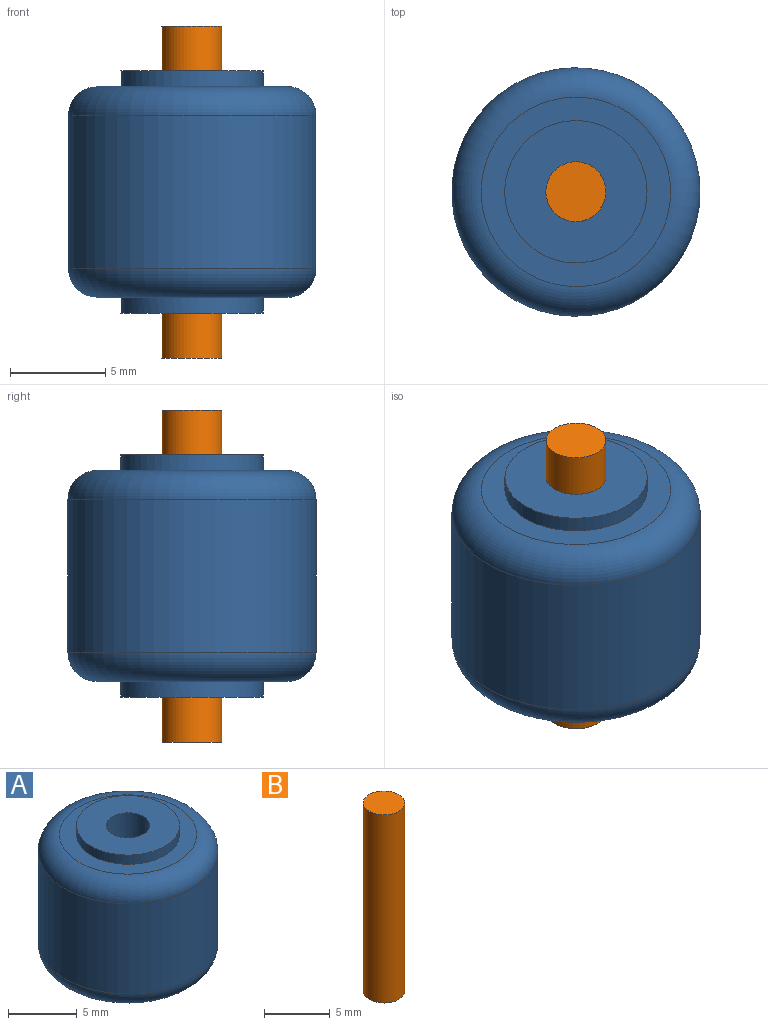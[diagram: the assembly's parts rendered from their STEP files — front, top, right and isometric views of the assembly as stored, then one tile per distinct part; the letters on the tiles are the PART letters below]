
ASSEMBLY  parts=2 mates=1
PART A: 10 faces, bbox 14.1x14.1x12.7 mm
  f0: cylinder r=6.52mm len=13.05mm, axis (0,0,-1), area 328.5mm2, adj f3,f4
  f1: plane 9.96x9.96mm, normal (0,0,1), area 34mm2, adj f4,f7
  f2: plane 9.96x9.96mm, normal (0,0,-1), area 34mm2, adj f3,f5
  f3: torus R=4.98mm, axis (0,0,1), area 90.8mm2, adj f0,f2
  f4: torus R=4.98mm, axis (0,0,1), area 90.8mm2, adj f0,f1
  f5: cylinder r=3.74mm len=7.48mm, axis (0,0,1), area 19.1mm2, adj f2,f6
  f6: plane 7.48x7.48mm, normal (0,0,-1), area 36.1mm2, adj f5,f9
  f7: cylinder r=3.74mm len=7.48mm, axis (0,0,-1), area 19.1mm2, adj f1,f8
  f8: plane 7.48x7.48mm, normal (0,0,1), area 36.1mm2, adj f7,f9
  f9: cylinder r=1.57mm len=12.73mm, axis (0,0,1), area 125.9mm2, adj f6,f8
PART B: 3 faces, bbox 3.1x3.1x17.4 mm
  f0: cylinder r=1.57mm len=17.45mm, axis (0,0,1), area 172.7mm2, adj f1,f2
  f1: plane 3.15x3.15mm, normal (0,0,-1), area 7.8mm2, adj f0
  f2: plane 3.15x3.15mm, normal (0,0,1), area 7.8mm2, adj f0
PLACE A at identity
PLACE B t=(-3.31,-15.27,14.27)mm
MATE revolute B.f0 <-> A.f0  axis (0,0,1) through (-57.65,-13.78,14.27)mm
